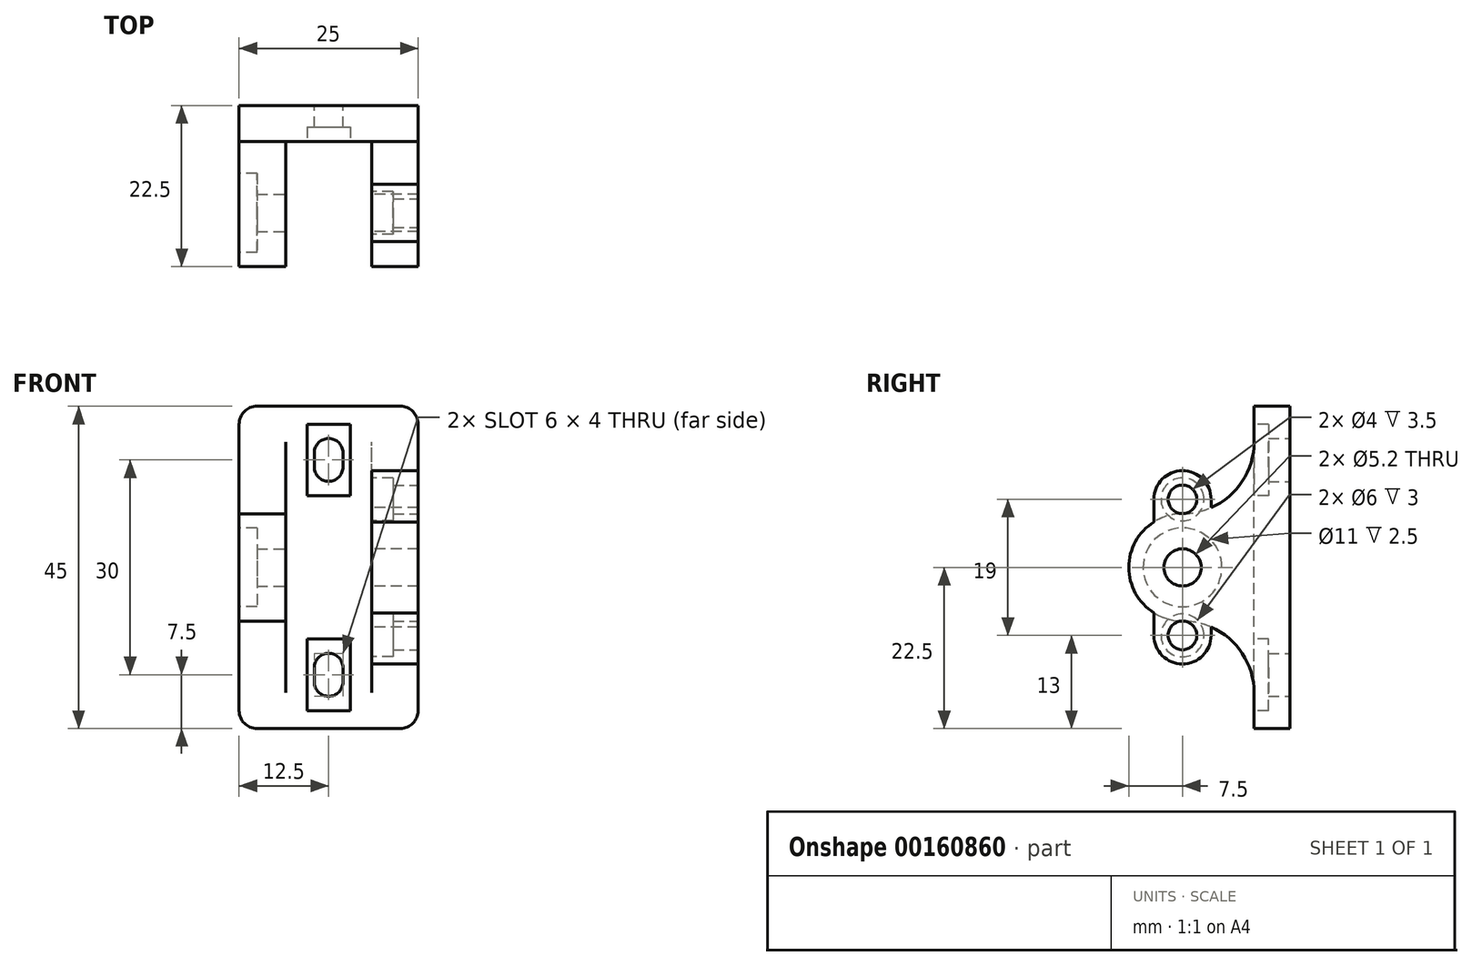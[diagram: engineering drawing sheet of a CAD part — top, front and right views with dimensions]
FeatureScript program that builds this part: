
annotation { "Feature Type Name" : "Feature", "Feature Type Description" : "" }
export const myFeature = defineFeature(function(context is Context, id is Id, definition is map)
    precondition{}
    {
        {
            var Q0;
            Q0=qCreatedBy(makeId("Front.planeOp"),FACE);
            var sketch = newSketch(context, id + "F0", { "sketchPlane" : qUnion([Q0])});
            skLineSegment(sketch, "E0.bottom", {"start": v(-10, 22.5) * mm, "end": v(10, 22.5) * mm});
            skLineSegment(sketch, "E0.top", {"start": v(-10, -22.5) * mm, "end": v(10, -22.5) * mm});
            skLineSegment(sketch, "E0.left", {"start": v(-12.5, 20) * mm, "end": v(-12.5, -20) * mm});
            skLineSegment(sketch, "E0.right", {"start": v(12.5, 20) * mm, "end": v(12.5, -20) * mm});
            skLineSegment(sketch, "E1", {"start": v(0, 22.5) * mm, "end": v(0, 0) * mm, "construction": true});
            skLineSegment(sketch, "E2", {"start": v(0, 0) * mm, "end": v(-12.5, 0) * mm, "construction": true});
            skLineSegment(sketch, "E3", {"start": v(2, -14) * mm, "end": v(2, -16) * mm});
            skLineSegment(sketch, "E4.MirrorCS", {"start": v(-2, -14) * mm, "end": v(-2, -16) * mm});
            skArc(sketch, "E5", {"start": v(2, -14) * mm, "mid": v(0, -12) * mm, "end": v(-2, -14) * mm});
            skArc(sketch, "E6", {"start": v(-2, -16) * mm, "mid": v(0, -18) * mm, "end": v(2, -16) * mm});
            skPoint(sketch, "E7", {"position": v(-2, -15) * mm});
            skPoint(sketch, "E8.MirrorP", {"position": v(-2, 15) * mm});
            skLineSegment(sketch, "E9.MirrorCS", {"start": v(-2, 14) * mm, "end": v(-2, 16) * mm});
            skArc(sketch, "E10.MirrorCS", {"start": v(2, 14) * mm, "mid": v(0, 12) * mm, "end": v(-2, 14) * mm});
            skLineSegment(sketch, "E11.MirrorCS", {"start": v(2, 14) * mm, "end": v(2, 16) * mm});
            skArc(sketch, "E12.MirrorCS", {"start": v(-2, 16) * mm, "mid": v(0, 18) * mm, "end": v(2, 16) * mm});
            skLineSegment(sketch, "E13", {"start": v(6, 22.5) * mm, "end": v(6, -22.5) * mm, "construction": true});
            skLineSegment(sketch, "E14.MirrorCS", {"start": v(-6, 22.5) * mm, "end": v(-6, -22.5) * mm, "construction": true});
            skPoint(sketch, "E15.visualSharp", {"position": v(-12.5, 22.5) * mm});
            skArc(sketch, "E15.filletArc", {"start": v(-10, 22.5) * mm, "mid": v(-11.77, 21.77) * mm, "end": v(-12.5, 20) * mm});
            skPoint(sketch, "E16.visualSharp", {"position": v(12.5, 22.5) * mm});
            skArc(sketch, "E16.filletArc", {"start": v(12.5, 20) * mm, "mid": v(11.77, 21.77) * mm, "end": v(10, 22.5) * mm});
            skPoint(sketch, "E17.visualSharp", {"position": v(12.5, -22.5) * mm});
            skArc(sketch, "E17.filletArc", {"start": v(10, -22.5) * mm, "mid": v(11.77, -21.77) * mm, "end": v(12.5, -20) * mm});
            skPoint(sketch, "E18.visualSharp", {"position": v(-12.5, -22.5) * mm});
            skArc(sketch, "E18.filletArc", {"start": v(-12.5, -20) * mm, "mid": v(-11.77, -21.77) * mm, "end": v(-10, -22.5) * mm});
            skPoint(sketch, "E19", {"position": v(6, 0) * mm});
            skSolve(sketch);
        }
        {
            var Q0;
            Q0 = qSketchRegion(id + "F0", true);
            extrude(context, id + "F1", {"entities" : qUnion([Q0]), "depth" : 5 * mm, "offsetDistance" : 25 * mm});
        }
        {
            var Q0;
            Q0=makeQuery(id+"F1.opExtrude","CAP_FACE",FACE,{"disambiguationData":[OSD([sQuery(id+"F0.wireOp",EDGE,"E0.bottom"),sQuery(id+"F0.wireOp",EDGE,"E0.top"),sQuery(id+"F0.wireOp",EDGE,"E0.left"),sQuery(id+"F0.wireOp",EDGE,"E0.right"),sQuery(id+"F0.wireOp",EDGE,"E3"),sQuery(id+"F0.wireOp",EDGE,"E4.MirrorCS"),sQuery(id+"F0.wireOp",EDGE,"E5"),sQuery(id+"F0.wireOp",EDGE,"E6"),sQuery(id+"F0.wireOp",EDGE,"E9.MirrorCS"),sQuery(id+"F0.wireOp",EDGE,"E10.MirrorCS"),sQuery(id+"F0.wireOp",EDGE,"E11.MirrorCS"),sQuery(id+"F0.wireOp",EDGE,"E12.MirrorCS"),sQuery(id+"F0.wireOp",EDGE,"E15.filletArc"),sQuery(id+"F0.wireOp",EDGE,"E16.filletArc"),sQuery(id+"F0.wireOp",EDGE,"E17.filletArc"),sQuery(id+"F0.wireOp",EDGE,"E18.filletArc")])],"isStart":false});
            var sketch = newSketch(context, id + "F2", { "sketchPlane" : qUnion([Q0])});
            skLineSegment(sketch, "E20.bottom", {"start": v(-3, 20) * mm, "end": v(3, 20) * mm});
            skLineSegment(sketch, "E20.top", {"start": v(-3, 10) * mm, "end": v(3, 10) * mm});
            skLineSegment(sketch, "E20.left", {"start": v(-3, 20) * mm, "end": v(-3, 10) * mm});
            skLineSegment(sketch, "E20.right", {"start": v(3, 20) * mm, "end": v(3, 10) * mm});
            skPoint(sketch, "E21", {"position": v(0, 16) * mm});
            skPoint(sketch, "E22", {"position": v(0, 14) * mm});
            skLineSegment(sketch, "E23", {"start": v(0, 16) * mm, "end": v(0, 20) * mm, "construction": true});
            skLineSegment(sketch, "E24", {"start": v(0, 16) * mm, "end": v(0, 14) * mm, "construction": true});
            skLineSegment(sketch, "E25", {"start": v(0, 15) * mm, "end": v(-3, 15) * mm, "construction": true});
            skLineSegment(sketch, "E26.MirrorCS", {"start": v(-3, -10) * mm, "end": v(3, -10) * mm});
            skLineSegment(sketch, "E27.MirrorCS", {"start": v(3, -20) * mm, "end": v(3, -10) * mm});
            skLineSegment(sketch, "E28.MirrorCS", {"start": v(-3, -20) * mm, "end": v(3, -20) * mm});
            skLineSegment(sketch, "E29.MirrorCS", {"start": v(-3, -20) * mm, "end": v(-3, -10) * mm});
            skSolve(sketch);
        }
        {
            var Q0;
            Q0 = qSketchRegion(id + "F2", true);
            extrude(context, id + "F3", {"entities" : qUnion([Q0]), "operationType" : NewBodyOperationType.REMOVE, "oppositeDirection" : true, "depth" : 2 * mm, "offsetDistance" : 25 * mm});
        }
        {
            var Q0;
            Q0=qCreatedBy(makeId("Right.planeOp"),FACE);
            var sketch = newSketch(context, id + "F4", { "sketchPlane" : qUnion([Q0])});
            skCircle(sketch, "E30", {"center": v(-15, 0) * mm, "radius": 2.6 * mm});
            skArc(sketch, "E31", {"start": v(-15, 7.5) * mm, "mid": v(-22.5, 0) * mm, "end": v(-15, -7.5) * mm});
            skArc(sketch, "E32", {"start": v(-15, 7.5) * mm, "mid": v(-7.93, 10.43) * mm, "end": v(-5, 17.5) * mm});
            skArc(sketch, "E33.MirrorCS", {"start": v(-15, -7.5) * mm, "mid": v(-7.93, -10.43) * mm, "end": v(-5, -17.5) * mm});
            skLineSegment(sketch, "E34", {"start": v(-5, -17.5) * mm, "end": v(-5, 17.5) * mm});
            skSolve(sketch);
        }
        {
            var Q0;
            Q0 = qSketchRegion(id + "F4", true);
            var Q1;
            Q1=makeQuery(id+"F1.opExtrude","SWEPT_FACE",FACE,{"disambiguationData":[OSD([sQuery(id+"F0.wireOp",EDGE,"E0.right")])]});
            extrude(context, id + "F5", {"entities" : qUnion([Q0]), "operationType" : NewBodyOperationType.ADD, "endBound" : BoundingType.UP_TO_SURFACE, "depth" : 25 * mm, "endBoundEntityFace" : qUnion([Q1]), "offsetDistance" : 25 * mm, "hasSecondDirection" : true, "secondDirectionOppositeDirection" : false, "secondDirectionDepth" : 6 * mm});
        }
        {
            var Q0;
            Q0 = qSketchRegion(id + "F4", true);
            var Q1;
            Q1=makeQuery(id+"F1.opExtrude","SWEPT_FACE",FACE,{"disambiguationData":[OSD([sQuery(id+"F0.wireOp",EDGE,"E0.left")])]});
            extrude(context, id + "F6", {"entities" : qUnion([Q0]), "operationType" : NewBodyOperationType.ADD, "endBound" : BoundingType.UP_TO_SURFACE, "oppositeDirection" : true, "depth" : 25 * mm, "endBoundEntityFace" : qUnion([Q1]), "offsetDistance" : 25 * mm, "hasSecondDirection" : true, "secondDirectionOppositeDirection" : false, "secondDirectionDepth" : -6 * mm});
        }
        {
            var Q0;
            {var subQ0=sQuery(id+"F0.wireOp",EDGE,"E0.left");Q0=makeQuery(id+"F6.boolean.opBoolean","MERGE",FACE,{"derivedFrom":[makeQuery(id+"F1.opExtrude","SWEPT_FACE",FACE,{"disambiguationData":[OSD([subQ0])]}),makeQuery(id+"F6.opExtrude","CAP_FACE",FACE,{"disambiguationData":[OSD([subQ0])],"isStart":false})]});}
            var sketch = newSketch(context, id + "F7", { "sketchPlane" : qUnion([Q0])});
            skCircle(sketch, "E35", {"center": v(15, 0) * mm, "radius": 5.5 * mm});
            skSolve(sketch);
        }
        {
            var Q0;
            Q0 = qSketchRegion(id + "F7", true);
            extrude(context, id + "F8", {"entities" : qUnion([Q0]), "operationType" : NewBodyOperationType.REMOVE, "oppositeDirection" : true, "depth" : 2.5 * mm, "offsetDistance" : 25 * mm});
        }
        {
            var Q0;
            {var subQ0=sQuery(id+"F0.wireOp",EDGE,"E0.right");Q0=makeQuery(id+"F5.boolean.opBoolean","MERGE",FACE,{"derivedFrom":[makeQuery(id+"F1.opExtrude","SWEPT_FACE",FACE,{"disambiguationData":[OSD([subQ0])]}),makeQuery(id+"F5.opExtrude","CAP_FACE",FACE,{"disambiguationData":[OSD([subQ0])],"isStart":false})]});}
            var sketch = newSketch(context, id + "F9", { "sketchPlane" : qUnion([Q0])});
            skArc(sketch, "E36", {"start": v(-11, 9.5) * mm, "mid": v(-15, 13.5) * mm, "end": v(-19, 9.5) * mm});
            skLineSegment(sketch, "E37", {"start": v(-19, 9.5) * mm, "end": v(-19, 2.6) * mm});
            skLineSegment(sketch, "E38", {"start": v(-11, 9.5) * mm, "end": v(-11, 2.6) * mm});
            skCircle(sketch, "E39", {"center": v(-15, 9.5) * mm, "radius": 2 * mm});
            skLineSegment(sketch, "E40.MirrorCS", {"start": v(-19, -9.5) * mm, "end": v(-19, -2.6) * mm});
            skArc(sketch, "E41.MirrorCS", {"start": v(-11, -9.5) * mm, "mid": v(-15, -13.5) * mm, "end": v(-19, -9.5) * mm});
            skCircle(sketch, "E42.MirrorC", {"center": v(-15, -9.5) * mm, "radius": 2 * mm});
            skLineSegment(sketch, "E43.MirrorCS", {"start": v(-11, -9.5) * mm, "end": v(-11, -2.6) * mm});
            skLineSegment(sketch, "E44", {"start": v(-19, 2.6) * mm, "end": v(-11, 2.6) * mm});
            skLineSegment(sketch, "E45", {"start": v(-11, -2.6) * mm, "end": v(-19, -2.6) * mm});
            skPoint(sketch, "E46", {"position": v(-15, 0) * mm});
            skSolve(sketch);
        }
        {
            var Q0;
            Q0 = qSketchRegion(id + "F9", true);
            var Q1;
            Q1=makeQuery(id+"F5.opExtrude","CAP_FACE",FACE,{"disambiguationData":[OSD([sQuery(id+"F4.wireOp",EDGE,"E30"),sQuery(id+"F4.wireOp",EDGE,"E31"),sQuery(id+"F4.wireOp",EDGE,"E32"),sQuery(id+"F4.wireOp",EDGE,"E33.MirrorCS"),sQuery(id+"F4.wireOp",EDGE,"E34")])],"isStart":true});
            extrude(context, id + "F10", {"entities" : qUnion([Q0]), "operationType" : NewBodyOperationType.ADD, "endBound" : BoundingType.UP_TO_SURFACE, "oppositeDirection" : true, "depth" : 25 * mm, "endBoundEntityFace" : qUnion([Q1]), "offsetDistance" : 25 * mm});
        }
        {
            var Q0;
            {var subQ0=sQuery(id+"F4.wireOp",EDGE,"E34");var subQ1=sQuery(id+"F4.wireOp",EDGE,"E33.MirrorCS");var subQ2=sQuery(id+"F4.wireOp",EDGE,"E32");var subQ3=sQuery(id+"F4.wireOp",EDGE,"E31");var subQ4=sQuery(id+"F4.wireOp",EDGE,"E30");Q0=makeQuery(id+"F10.boolean.opBoolean","MERGE",FACE,{"derivedFrom":[makeQuery(id+"F5.opExtrude","CAP_FACE",FACE,{"disambiguationData":[OSD([subQ4,subQ3,subQ2,subQ1,subQ0])],"isStart":true}),makeQuery(id+"F10.opExtrude","CAP_FACE",FACE,{"disambiguationData":[OSD([subQ4,subQ3,subQ2,subQ1,subQ0]),OD(0.0)],"isStart":false}),makeQuery(id+"F10.opExtrude","CAP_FACE",FACE,{"disambiguationData":[OSD([subQ4,subQ3,subQ2,subQ1,subQ0]),OD(1.0)],"isStart":false})]});}
            var sketch = newSketch(context, id + "F11", { "sketchPlane" : qUnion([Q0])});
            skCircle(sketch, "E47", {"center": v(15, 9.5) * mm, "radius": 3 * mm});
            skCircle(sketch, "E48", {"center": v(15, -9.5) * mm, "radius": 3 * mm});
            skSolve(sketch);
        }
        {
            var Q0;
            Q0 = qSketchRegion(id + "F11", true);
            extrude(context, id + "F12", {"entities" : qUnion([Q0]), "operationType" : NewBodyOperationType.REMOVE, "oppositeDirection" : true, "depth" : 3 * mm, "offsetDistance" : 25 * mm});
        }
    });
